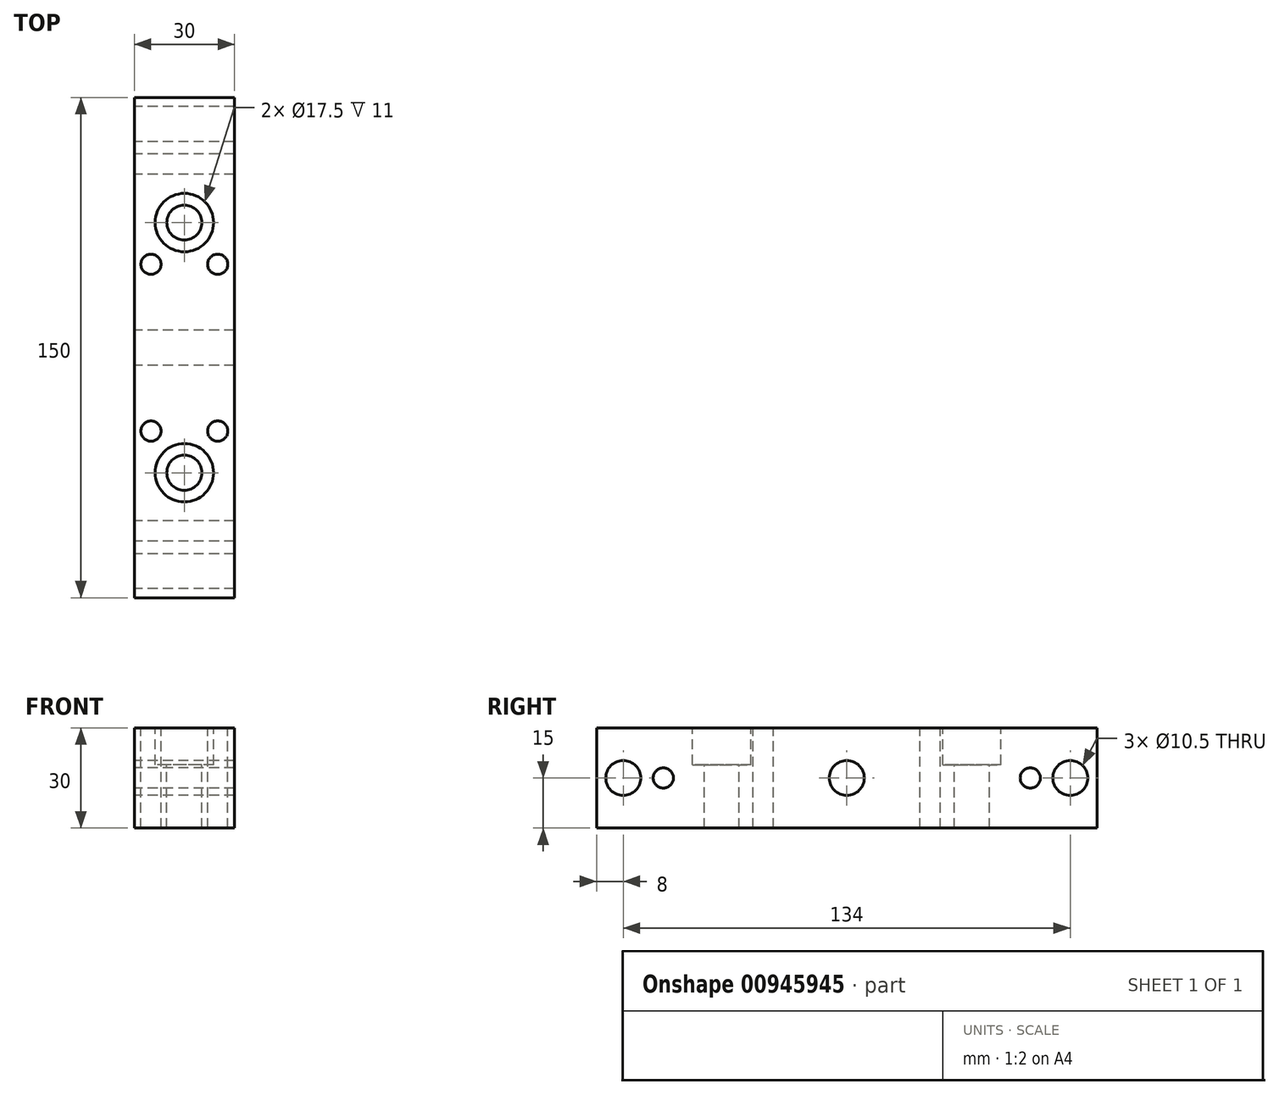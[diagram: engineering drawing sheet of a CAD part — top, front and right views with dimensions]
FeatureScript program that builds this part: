
annotation { "Feature Type Name" : "Feature", "Feature Type Description" : "" }
export const myFeature = defineFeature(function(context is Context, id is Id, definition is map)
    precondition{}
    {
        {
            var Q0;
            Q0=qCreatedBy(makeId("Front.planeOp"),FACE);
            var sketch = newSketch(context, id + "F0", { "sketchPlane" : qUnion([Q0])});
            skLineSegment(sketch, "E0.bottom", {"start": v(15, -15) * mm, "end": v(-15, -15) * mm});
            skLineSegment(sketch, "E0.top", {"start": v(15, 15) * mm, "end": v(-15, 15) * mm});
            skLineSegment(sketch, "E0.left", {"start": v(15, -15) * mm, "end": v(15, 15) * mm});
            skLineSegment(sketch, "E0.right", {"start": v(-15, -15) * mm, "end": v(-15, 15) * mm});
            skPoint(sketch, "E0.middle", {"position": v(0, 0) * mm});
            skSolve(sketch);
        }
        {
            var Q0;
            Q0 = qSketchRegion(id + "F0", true);
            extrude(context, id + "F1", {"entities" : qUnion([Q0]), "depth" : 150 * mm, "offsetDistance" : 25 * mm});
        }
        {
            var Q0;
            Q0=makeQuery(id+"F1.opExtrude","SWEPT_FACE",FACE,{"disambiguationData":[OSD([sQuery(id+"F0.wireOp",EDGE,"E0.right")])]});
            var sketch = newSketch(context, id + "F2", { "sketchPlane" : qUnion([Q0])});
            skCircle(sketch, "E1", {"center": v(8, 0) * mm, "radius": 5.25 * mm});
            skCircle(sketch, "E2", {"center": v(75, 0) * mm, "radius": 5.25 * mm});
            skPoint(sketch, "E2.centerSnap0", {"position": v(75, 15) * mm});
            skLineSegment(sketch, "E3", {"start": v(75, 0) * mm, "end": v(75, 15) * mm, "construction": true});
            skCircle(sketch, "E4.MirrorC", {"center": v(142, 0) * mm, "radius": 5.25 * mm});
            skSolve(sketch);
        }
        {
            var Q0;
            Q0 = qSketchRegion(id + "F2", true);
            extrude(context, id + "F3", {"entities" : qUnion([Q0]), "operationType" : NewBodyOperationType.REMOVE, "endBound" : BoundingType.THROUGH_ALL, "oppositeDirection" : true, "depth" : 25 * mm, "offsetDistance" : 25 * mm});
        }
        {
            var Q0;
            Q0=makeQuery(id+"F1.opExtrude","SWEPT_FACE",FACE,{"disambiguationData":[OSD([sQuery(id+"F0.wireOp",EDGE,"E0.top")])]});
            var sketch = newSketch(context, id + "F4", { "sketchPlane" : qUnion([Q0])});
            skCircle(sketch, "E5", {"center": v(0, -37.5) * mm, "radius": 5.25 * mm});
            skCircle(sketch, "E6", {"center": v(10, -50) * mm, "radius": 3.04 * mm});
            skLineSegment(sketch, "E7", {"start": v(15, -75) * mm, "end": v(-15, -75) * mm, "construction": true});
            skCircle(sketch, "E8.MirrorC", {"center": v(0, -112.5) * mm, "radius": 5.25 * mm});
            skCircle(sketch, "E9.MirrorC", {"center": v(10, -100) * mm, "radius": 3.04 * mm});
            skLineSegment(sketch, "E10", {"start": v(0, -75) * mm, "end": v(0, -150) * mm, "construction": true});
            skCircle(sketch, "E11.MirrorC", {"center": v(-10, -50) * mm, "radius": 3.04 * mm});
            skCircle(sketch, "E12.MirrorC", {"center": v(-10, -100) * mm, "radius": 3.04 * mm});
            skSolve(sketch);
        }
        {
            var Q0;
            Q0 = qSketchRegion(id + "F4", true);
            extrude(context, id + "F5", {"entities" : qUnion([Q0]), "operationType" : NewBodyOperationType.REMOVE, "endBound" : BoundingType.THROUGH_ALL, "oppositeDirection" : true, "depth" : 25 * mm, "offsetDistance" : 25 * mm});
        }
        {
            var Q0;
            Q0=makeQuery(id+"F1.opExtrude","SWEPT_FACE",FACE,{"disambiguationData":[OSD([sQuery(id+"F0.wireOp",EDGE,"E0.top")])]});
            var sketch = newSketch(context, id + "F6", { "sketchPlane" : qUnion([Q0])});
            skCircle(sketch, "E13", {"center": v(0, -37.5) * mm, "radius": 8.75 * mm});
            skLineSegment(sketch, "E14", {"start": v(15, -75) * mm, "end": v(-15, -75) * mm, "construction": true});
            skCircle(sketch, "E15.MirrorC", {"center": v(0, -112.5) * mm, "radius": 8.75 * mm});
            skSolve(sketch);
        }
        {
            var Q0;
            Q0 = qSketchRegion(id + "F6", true);
            extrude(context, id + "F7", {"entities" : qUnion([Q0]), "operationType" : NewBodyOperationType.REMOVE, "oppositeDirection" : true, "depth" : 11 * mm, "offsetDistance" : 25 * mm});
        }
        {
            var Q0;
            Q0=makeQuery(id+"F1.opExtrude","SWEPT_FACE",FACE,{"disambiguationData":[OSD([sQuery(id+"F0.wireOp",EDGE,"E0.right")])]});
            var sketch = newSketch(context, id + "F8", { "sketchPlane" : qUnion([Q0])});
            skCircle(sketch, "E16", {"center": v(20, 0) * mm, "radius": 3.04 * mm});
            skLineSegment(sketch, "E17", {"start": v(75, -15) * mm, "end": v(75, 15) * mm, "construction": true});
            skCircle(sketch, "E18.MirrorC", {"center": v(130, 0) * mm, "radius": 3.04 * mm});
            skSolve(sketch);
        }
        {
            var Q0;
            Q0 = qSketchRegion(id + "F8", true);
            extrude(context, id + "F9", {"entities" : qUnion([Q0]), "operationType" : NewBodyOperationType.REMOVE, "endBound" : BoundingType.THROUGH_ALL, "oppositeDirection" : true, "depth" : 25 * mm, "offsetDistance" : 25 * mm});
        }
    });
